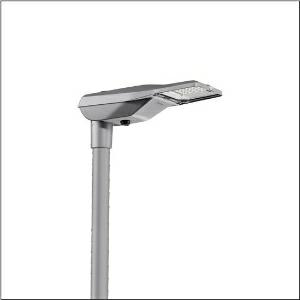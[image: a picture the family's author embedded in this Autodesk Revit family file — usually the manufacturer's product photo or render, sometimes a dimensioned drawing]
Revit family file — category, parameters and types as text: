
# Revit family: streetlight_sl_21_iq_micro___st1_0a_5xe1d31u08db_5c5a
name_source: partatom
category: Lighting Fixtures
units: mm (PartAtom-declared; Revit-internal decimal feet)

## family parameters
Cut with Voids When Loaded = No
Host = Face
Light Source = No
Part Type = Normal
Room Calculation Point = No
Round Connector Dimension = Use Diameter
Shared = No

## types (1)
- --- (1 x LED, 5110 lm, 39.1 W, 3000K)
    Apparent Load = 39 VA
    CIE Flux Codes = 37 72 97 100 100
    Color Rendering = 70
    Color Temperature = 3000K
    Default Elevation = 1800 mm
    Description = Streetlight SL 21 iQ micro, mast luminaire, primary light control with lens, of PMMA, primary optical cover: cover, of toughened safety glass, transparent, light distribution: ST1.0a, light emission: direct distribution, primary light characteristic: asymmetric, installation type: post-top, side-entry, LED, High Power LED, rated luminous flux: 5.110lm, luminous efficacy: 131lm/W, light colour: 730, colour temperature: 3000K, control gear: iQ-Street Remote, D4i with power reduction, control: pre-setting: logarithmic dimming characteristic, Street-Remote, Auto-Match, Temp-Guard, Lumen-Switch, Night-Set, Smart-Wire, Light-Fading, Desk-Remote (wireless, voltage-free reading and setting of iQ features in the workshop via application-optimized NFC function/RFID function), optimised constant luminous flux control (CLO 2.0), mains connection: 220..240V, AC, 50/60Hz, start of lifetime: 39W, end of service life: 41W, reduction: 17W, luminaire housing, of diecast aluminium, powder-coated, Siteco® metallic grey (DB 702S), corrosivity category C5 mid according to DIN EN ISO 12944, please order mast flange separately, inclination adjustable: 0°, 5°, 10°, 15°, sealing non-destructively replaceable, multi-level sealing system, length: 528mm, width: 235mm, height: 110mm, mast flange for spigot size: 42mm (side-entry): 5XC10008XM4, 60/48mm (side-entry/post-top): 5XC10108XM2, 76/60mm (side-entry/post-top): 5XC10108XM1, mounting height: 4..8m, Smart Interface below, protection rating (complete): IP66, insulation class (complete): insulation class II (safety insulation), certification: CE, ENEC, ENEC+, VDE, impact resistance: IK10, permissible operating ambient temperature for outdoor applications: -40..+50°C, standard-compliant lighting for roads and squares, packaging unit: 1 piece

Light Distribution: ST1.0a
    Height = 110 mm
    Lamp = 1 x LED
    Lamp Light Flux = 5110 lm
    Lamp Power = 39.1 W
    Lamp count = 1
    Length = 528 mm
    Luminous efficacy = 131 lm/W
    Manufacturer = Siteco
    ModVariant = No
    Model = 5XE1D31U08DB
    Number of Poles = 1
    OnlyDefault = Yes
    Power Factor = 1
    Product Name = Streetlight SL 21 iQ micro | ST1.0a
    Product group = mast luminaire | pylon top
    ProductGroupID = 6100
    Protection Class = Protection class II
    Protection Degree = IP 66
    RLX_Detail_Level = 1
    RLX_Emergency_Light_Flux = 0 lm
    RLX_Emergency_Type = 0
    RLX_Emergency_Type_DB = No
    RlxData = <blob elided: 99713 chars, md5=865f1bb3>
    Socket = socket
    Standby Power = 0 W
    System Light Flux = 5110 lm
    System Power = 39 W
    Type Comments = factory setting: luminous flux: 100 % | dim-lin: 254 | 765 mA
    Type Image = l_1277290.jpg
    URL = http://relux.com
    VarID = @adj_137199
    Voltage = 0 V
    Weight = 0.00 kg
    Width = 235 mm

## geometry (parser evidence)
native form markers: Blend x4, Sweep x13
no freeform markers — native parametric forms only
